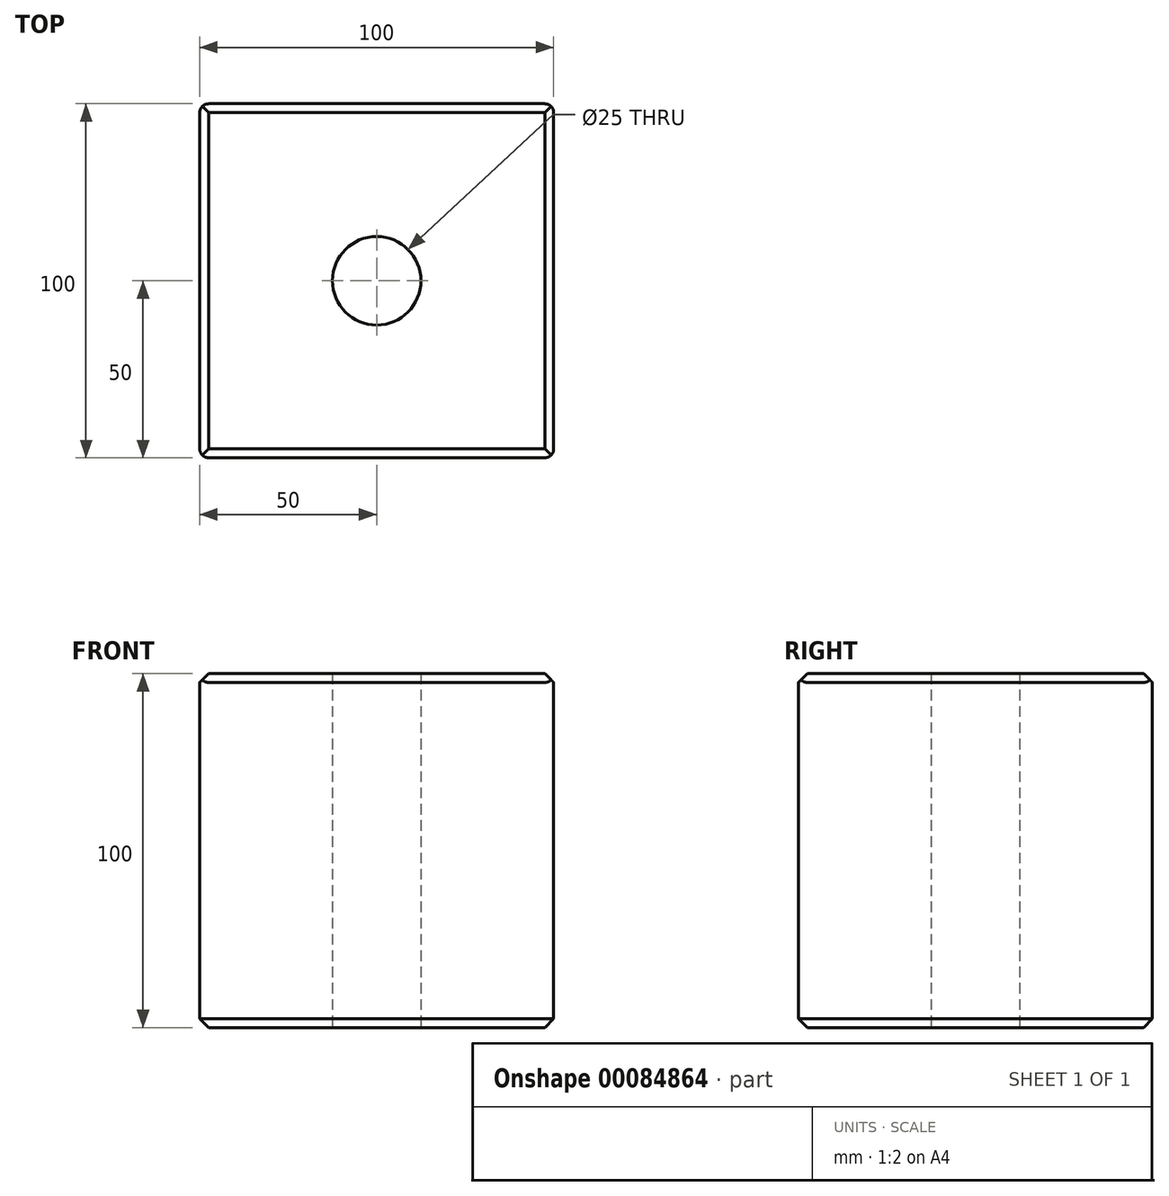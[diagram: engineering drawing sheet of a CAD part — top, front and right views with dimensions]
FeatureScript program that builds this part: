
annotation { "Feature Type Name" : "Feature", "Feature Type Description" : "" }
export const myFeature = defineFeature(function(context is Context, id is Id, definition is map)
    precondition{}
    {
        {
            var Q0;
            Q0=qCreatedBy(makeId("Front.planeOp"),FACE);
            var sketch = newSketch(context, id + "F0", { "sketchPlane" : qUnion([Q0])});
            skLineSegment(sketch, "E0.bottom", {"start": v(-50, 50) * mm, "end": v(50, 50) * mm});
            skLineSegment(sketch, "E0.top", {"start": v(-50, -50) * mm, "end": v(50, -50) * mm});
            skLineSegment(sketch, "E0.left", {"start": v(-50, 50) * mm, "end": v(-50, -50) * mm});
            skLineSegment(sketch, "E0.right", {"start": v(50, 50) * mm, "end": v(50, -50) * mm});
            skPoint(sketch, "E0.middle", {"position": v(0, 0) * mm});
            skSolve(sketch);
        }
        {
            var Q0;
            Q0=makeQuery(id+"F0.imprint","IMPRINT",FACE,{"disambiguationData":[TD([[makeQuery(id+"F0.imprint","IMPRINT",EDGE,{"derivedFrom":sQuery(id+"F0.wireOp",EDGE,"E0.bottom")}),-1.0]])]});
            extrude(context, id + "F1", {"entities" : qUnion([Q0]), "endBound" : BoundingType.SYMMETRIC, "depth" : 100 * mm});
        }
        {
            var Q0;
            Q0=makeQuery(id+"F1.opExtrude","SWEPT_EDGE",EDGE,{"disambiguationData":[OSD([sQuery(id+"F0.wireOp",EDGE,"E0.bottom"),sQuery(id+"F0.wireOp",EDGE,"E0.right")])]});
            var Q1;
            Q1=makeQuery(id+"F1.opExtrude","CAP_EDGE",EDGE,{"disambiguationData":[OSD([sQuery(id+"F0.wireOp",EDGE,"E0.bottom")])],"isStart":false});
            var Q2;
            Q2=makeQuery(id+"F1.opExtrude","SWEPT_EDGE",EDGE,{"disambiguationData":[OSD([sQuery(id+"F0.wireOp",EDGE,"E0.bottom"),sQuery(id+"F0.wireOp",EDGE,"E0.left")])]});
            var Q3;
            Q3=makeQuery(id+"F1.opExtrude","CAP_EDGE",EDGE,{"disambiguationData":[OSD([sQuery(id+"F0.wireOp",EDGE,"E0.bottom")])],"isStart":true});
            chamfer(context, id + "F2", {"entities" : qUnion([Q0, Q1, Q2, Q3]), "width" : 2.5 * mm, "tangentPropagation" : true});
        }
        {
            var Q0;
            Q0=makeQuery(id+"F1.opExtrude","CAP_EDGE",EDGE,{"disambiguationData":[OSD([sQuery(id+"F0.wireOp",EDGE,"E0.left")])],"isStart":true});
            var Q1;
            Q1=makeQuery(id+"F1.opExtrude","CAP_EDGE",EDGE,{"disambiguationData":[OSD([sQuery(id+"F0.wireOp",EDGE,"E0.right")])],"isStart":false});
            var Q2;
            Q2=makeQuery(id+"F1.opExtrude","CAP_EDGE",EDGE,{"disambiguationData":[OSD([sQuery(id+"F0.wireOp",EDGE,"E0.left")])],"isStart":false});
            var Q3;
            Q3=makeQuery(id+"F1.opExtrude","CAP_EDGE",EDGE,{"disambiguationData":[OSD([sQuery(id+"F0.wireOp",EDGE,"E0.right")])],"isStart":true});
            fillet(context, id + "F3", {"entities" : qUnion([Q0, Q1, Q2, Q3]), "radius" : 2.5 * mm, "tangentPropagation" : true, "allowEdgeOverflow" : false});
        }
        {
            var Q0;
            Q0=makeQuery(id+"F1.opExtrude","CAP_EDGE",EDGE,{"disambiguationData":[OSD([sQuery(id+"F0.wireOp",EDGE,"E0.top")])],"isStart":false});
            var Q1;
            Q1=makeQuery(id+"F1.opExtrude","CAP_EDGE",EDGE,{"disambiguationData":[OSD([sQuery(id+"F0.wireOp",EDGE,"E0.top")])],"isStart":true});
            var Q2;
            Q2=makeQuery(id+"F1.opExtrude","SWEPT_EDGE",EDGE,{"disambiguationData":[OSD([sQuery(id+"F0.wireOp",EDGE,"E0.top"),sQuery(id+"F0.wireOp",EDGE,"E0.left")])]});
            var Q3;
            Q3=makeQuery(id+"F1.opExtrude","SWEPT_EDGE",EDGE,{"disambiguationData":[OSD([sQuery(id+"F0.wireOp",EDGE,"E0.top"),sQuery(id+"F0.wireOp",EDGE,"E0.right")])]});
            chamfer(context, id + "F4", {"entities" : qUnion([Q0, Q1, Q2, Q3]), "width" : 2.5 * mm, "tangentPropagation" : true});
        }
        {
            var Q0;
            Q0=makeQuery(id+"F1.opExtrude","SWEPT_FACE",FACE,{"disambiguationData":[OSD([sQuery(id+"F0.wireOp",EDGE,"E0.top")])]});
            var sketch = newSketch(context, id + "F5", { "sketchPlane" : qUnion([Q0])});
            skCircle(sketch, "E1", {"center": v(0, 0) * mm, "radius": 12.5 * mm});
            skSolve(sketch);
        }
        {
            var Q0;
            Q0 = qSketchRegion(id + "F5", true);
            extrude(context, id + "F6", {"entities" : qUnion([Q0]), "operationType" : NewBodyOperationType.REMOVE, "endBound" : BoundingType.THROUGH_ALL, "oppositeDirection" : true, "depth" : 25.4 * mm});
        }
    });
